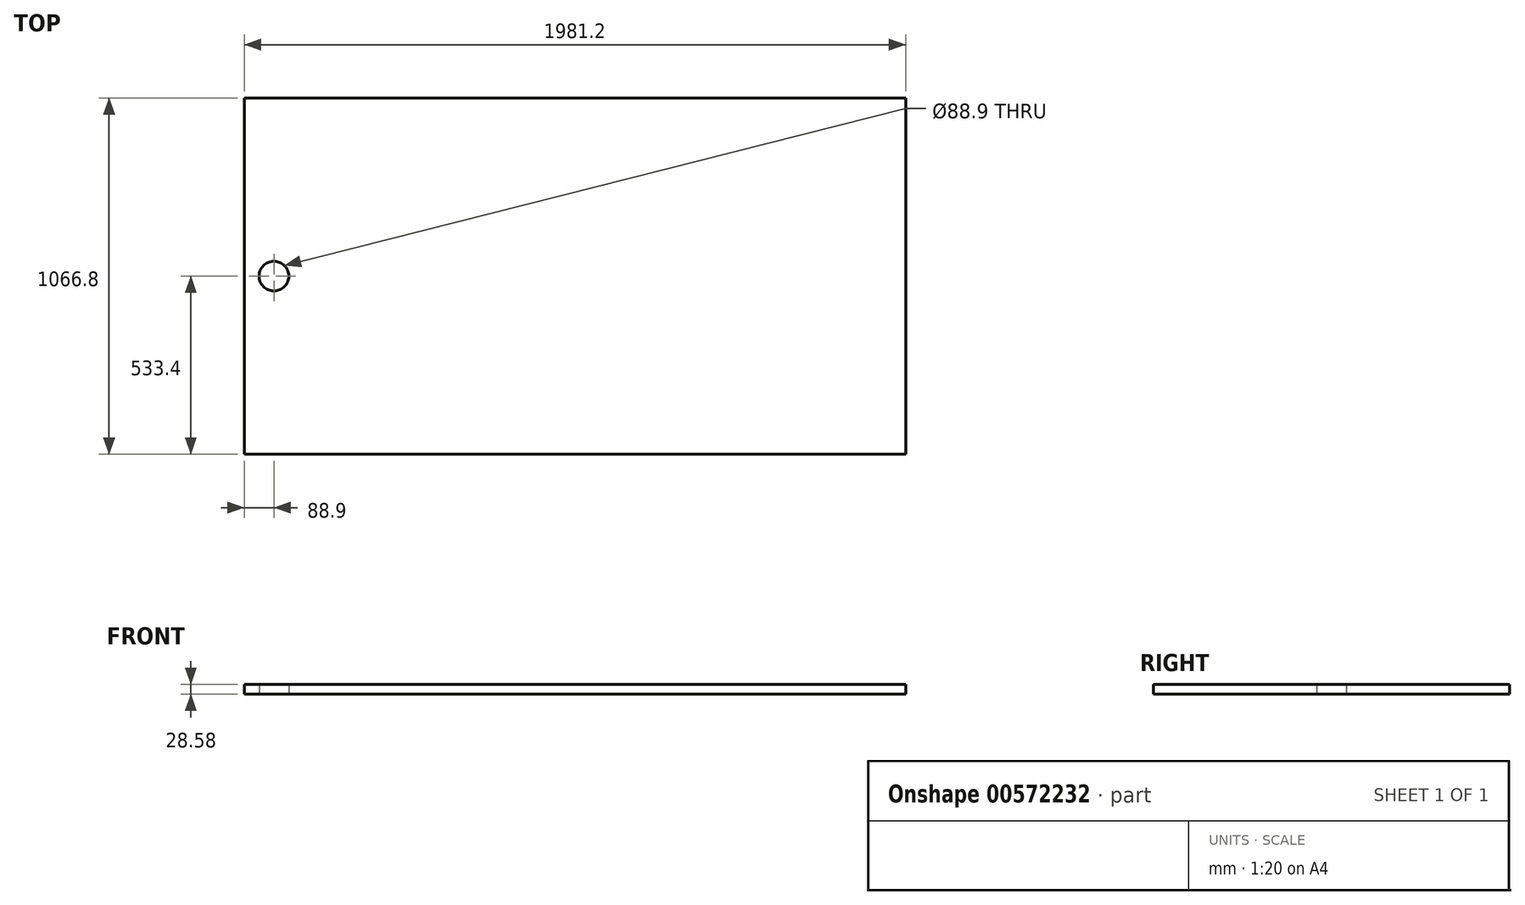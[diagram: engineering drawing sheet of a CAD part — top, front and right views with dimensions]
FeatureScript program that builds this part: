
annotation { "Feature Type Name" : "Feature", "Feature Type Description" : "" }
export const myFeature = defineFeature(function(context is Context, id is Id, definition is map)
    precondition{}
    {
        {
            var Q0;
            Q0=qCreatedBy(makeId("Top.planeOp"),FACE);
            var sketch = newSketch(context, id + "F0", { "sketchPlane" : qUnion([Q0])});
            skLineSegment(sketch, "E0.bottom", {"start": v(990.6, 533.4) * mm, "end": v(-990.6, 533.4) * mm});
            skLineSegment(sketch, "E0.top", {"start": v(990.6, -533.4) * mm, "end": v(-990.6, -533.4) * mm});
            skLineSegment(sketch, "E0.left", {"start": v(990.6, 533.4) * mm, "end": v(990.6, -533.4) * mm});
            skLineSegment(sketch, "E0.right", {"start": v(-990.6, 533.4) * mm, "end": v(-990.6, -533.4) * mm});
            skPoint(sketch, "E0.middle", {"position": v(0, 0) * mm});
            skLineSegment(sketch, "E1", {"start": v(-990.6, 0) * mm, "end": v(-901.7, 0) * mm});
            skPoint(sketch, "E1.endSnap0", {"position": v(-990.6, 0) * mm});
            skCircle(sketch, "E2", {"center": v(-901.7, 0) * mm, "radius": 44.45 * mm});
            skSolve(sketch);
        }
        {
            var Q0;
            {var subQ1=sQuery(id+"F0.wireOp",EDGE,"E0.bottom");Q0=makeQuery(id+"F0.imprint","IMPRINT",FACE,{"disambiguationData":[TD([[makeQuery(id+"F0.imprint","IMPRINT",EDGE,{"derivedFrom":subQ1}),1.0]])]});}
            extrude(context, id + "F1", {"entities" : qUnion([Q0]), "depth" : 28.57 * mm, "offsetDistance" : 25.4 * mm});
        }
    });
